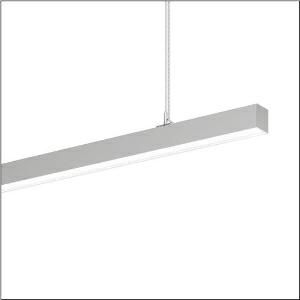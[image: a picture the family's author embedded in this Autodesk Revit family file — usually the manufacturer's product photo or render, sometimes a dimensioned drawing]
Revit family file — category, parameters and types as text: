
# Revit family: silica_r__21_51mx33tat7s_6391
name_source: partatom
category: Lighting Fixtures
units: mm (PartAtom-declared; Revit-internal decimal feet)

## family parameters
Cut with Voids When Loaded = No
Host = Face
Light Source = No
Part Type = Normal
Room Calculation Point = No
Round Connector Dimension = Use Diameter
Shared = No

## types (1)
- --- (1 x LED, 5740 lm, 53.8 W, 6500K)
    Apparent Load = 54 VA
    CIE Flux Codes = 78 96 99 56 100
    Color Rendering = 80
    Color Temperature = 6500K
    Default Elevation = 1800 mm
    Description = Silica® 21, office luminaire, primary optical cover: prismatic diffuser, of PMMA, CAT 2 (L<= 3000cd/m²), light emission: direct/indirect distribution, primary light characteristic: symmetric, installation type: suspended mounting, LED, rated luminous flux: 5.740lm, luminous efficacy: 102lm/W, light colour: 8tw, colour temperature: 2700..6500K, control gear: ECG DALI, with terminal, 3+2-pole, max. 2.5mm², mains connection: 220..240V, AC, 50/60Hz, rated input power: 56.5W, luminaire housing, of aluminium, metallic grey (RAL 9006), length: 1.204mm, width: 53mm, height: 53mm, protection rating (complete): IP20, insulation class (complete): insulation class I (protective earthing), certification: CE, permissible operating ambient temperature: 0..+35°C, standard: EN 50419, packaging unit: 1 piece
    Height = 53 mm
    Lamp = 1 x LED
    Lamp Light Flux = 5740 lm
    Lamp Power = 53.8 W
    Lamp count = 1
    Length = 1204 mm
    Luminous efficacy = 107 lm/W
    Manufacturer = Siteco
    ModVariant = No
    Model = 51MX33TAT7S
    Mounting Place = Ceiling
    Mounting Type = Pendant
    Number of Poles = 1
    OnlyDefault = Yes
    Power Factor = 1
    Product Name = Silica® 21
    Product group = office luminaire | ceiling pendant
    ProductGroupID = 902
    Protection Class = Protection class I
    Protection Degree = IP 20
    RLX_Detail_Level = 1
    RLX_Emergency_Light_Flux = 0 lm
    RLX_Emergency_Type = 0
    RLX_Emergency_Type_DB = No
    RlxData = <blob elided: 20209 chars, md5=3a9c649c>
    Socket = socket
    Standby Power = 0 W
    System Light Flux = 5740 lm
    System Power = 54 W
    Type Comments = individual setting
    Type Image = l_1335864.jpg
    URL = http://relux.com
    VarID = @adj_109549
    Voltage = 0 V
    Weight = 0.00 kg
    Width = 53 mm

## geometry (parser evidence)
native form markers: Blend x4, Sweep x11
no freeform markers — native parametric forms only
